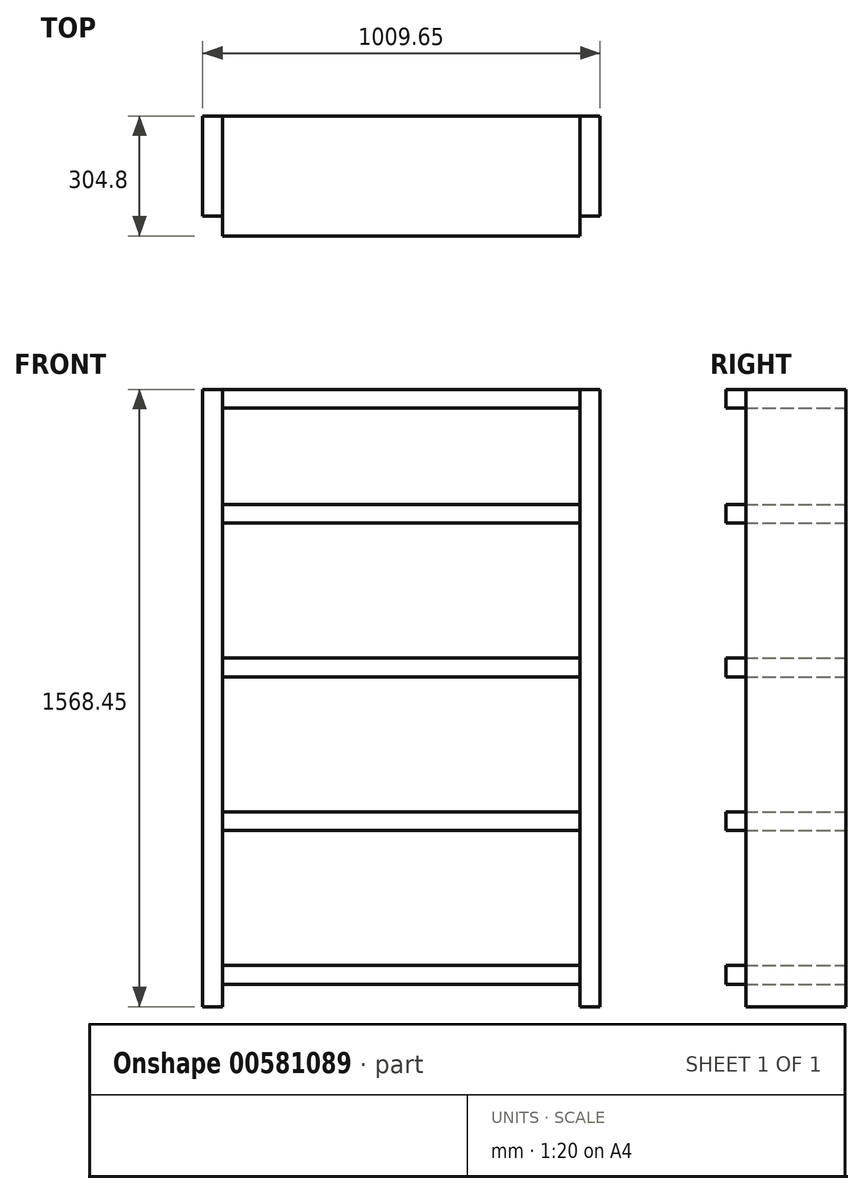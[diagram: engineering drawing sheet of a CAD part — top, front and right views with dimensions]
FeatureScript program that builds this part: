
annotation { "Feature Type Name" : "Feature", "Feature Type Description" : "" }
export const myFeature = defineFeature(function(context is Context, id is Id, definition is map)
    precondition{}
    {
        {
            var Q0;
            Q0=qCreatedBy(makeId("Front.planeOp"),FACE);
            var sketch = newSketch(context, id + "F0", { "sketchPlane" : qUnion([Q0])});
            skLineSegment(sketch, "E0.bottom", {"start": v(-778.9, 353.78) * mm, "end": v(-728.1, 353.78) * mm});
            skLineSegment(sketch, "E0.top", {"start": v(-778.9, -1214.67) * mm, "end": v(-728.1, -1214.67) * mm});
            skLineSegment(sketch, "E0.left", {"start": v(-778.9, 353.78) * mm, "end": v(-778.9, -1214.67) * mm});
            skLineSegment(sketch, "E0.right", {"start": v(-728.1, 353.78) * mm, "end": v(-728.1, -1214.67) * mm});
            skLineSegment(sketch, "E1.bottom", {"start": v(179.95, 353.78) * mm, "end": v(230.75, 353.78) * mm});
            skLineSegment(sketch, "E1.top", {"start": v(179.95, -1214.67) * mm, "end": v(230.75, -1214.67) * mm});
            skLineSegment(sketch, "E1.left", {"start": v(179.95, 353.78) * mm, "end": v(179.95, -1214.67) * mm});
            skLineSegment(sketch, "E1.right", {"start": v(230.75, 353.78) * mm, "end": v(230.75, -1214.67) * mm});
            skLineSegment(sketch, "E2.bottom", {"start": v(-728.1, 353.78) * mm, "end": v(179.95, 353.78) * mm});
            skLineSegment(sketch, "E2.top", {"start": v(-728.1, 306.16) * mm, "end": v(179.95, 306.16) * mm});
            skLineSegment(sketch, "E2.left", {"start": v(-728.1, 353.78) * mm, "end": v(-728.1, 306.16) * mm});
            skLineSegment(sketch, "E2.right", {"start": v(179.95, 353.78) * mm, "end": v(179.95, 306.16) * mm});
            skLineSegment(sketch, "E3.bottom", {"start": v(-728.1, -1109.9) * mm, "end": v(179.95, -1109.9) * mm});
            skLineSegment(sketch, "E3.top", {"start": v(-728.1, -1157.52) * mm, "end": v(179.95, -1157.52) * mm});
            skLineSegment(sketch, "E3.left", {"start": v(-728.1, -1109.9) * mm, "end": v(-728.1, -1157.52) * mm});
            skLineSegment(sketch, "E3.right", {"start": v(179.95, -1109.9) * mm, "end": v(179.95, -1157.52) * mm});
            skLineSegment(sketch, "E4.bottom", {"start": v(-728.1, -719.37) * mm, "end": v(179.95, -719.37) * mm});
            skLineSegment(sketch, "E4.top", {"start": v(-728.1, -767) * mm, "end": v(179.95, -767) * mm});
            skLineSegment(sketch, "E4.left", {"start": v(-728.1, -719.37) * mm, "end": v(-728.1, -767) * mm});
            skLineSegment(sketch, "E4.right", {"start": v(179.95, -719.37) * mm, "end": v(179.95, -767) * mm});
            skLineSegment(sketch, "E5.bottom", {"start": v(-728.1, -328.84) * mm, "end": v(179.95, -328.84) * mm});
            skLineSegment(sketch, "E5.top", {"start": v(-728.1, -376.47) * mm, "end": v(179.95, -376.47) * mm});
            skLineSegment(sketch, "E5.left", {"start": v(-728.1, -328.84) * mm, "end": v(-728.1, -376.47) * mm});
            skLineSegment(sketch, "E5.right", {"start": v(179.95, -328.84) * mm, "end": v(179.95, -376.47) * mm});
            skLineSegment(sketch, "E6.bottom", {"start": v(-728.1, 61.68) * mm, "end": v(179.95, 61.68) * mm});
            skLineSegment(sketch, "E6.top", {"start": v(-728.1, 14.06) * mm, "end": v(179.95, 14.06) * mm});
            skLineSegment(sketch, "E6.left", {"start": v(-728.1, 61.68) * mm, "end": v(-728.1, 14.06) * mm});
            skLineSegment(sketch, "E6.right", {"start": v(179.95, 61.68) * mm, "end": v(179.95, 14.06) * mm});
            skSolve(sketch);
        }
        {
            var Q0;
            Q0=makeQuery(id+"F0.imprint","IMPRINT",FACE,{"disambiguationData":[TD([[makeQuery(id+"F0.imprint","IMPRINT",EDGE,{"derivedFrom":sQuery(id+"F0.wireOp",EDGE,"E0.bottom")}),-1.0]])]});
            var Q1;
            Q1=makeQuery(id+"F0.imprint","IMPRINT",FACE,{"disambiguationData":[TD([[makeQuery(id+"F0.imprint","IMPRINT",EDGE,{"derivedFrom":sQuery(id+"F0.wireOp",EDGE,"E1.bottom")}),-1.0]])]});
            extrude(context, id + "F1", {"entities" : qUnion([Q0, Q1]), "depth" : 254 * mm, "offsetDistance" : 25.4 * mm});
        }
        {
            var Q0;
            Q0=makeQuery(id+"F0.imprint","IMPRINT",FACE,{"disambiguationData":[TD([[makeQuery(id+"F0.imprint","IMPRINT",EDGE,{"derivedFrom":sQuery(id+"F0.wireOp",EDGE,"E2.bottom")}),-1.0]])]});
            var Q1;
            Q1=makeQuery(id+"F0.imprint","IMPRINT",FACE,{"disambiguationData":[TD([[makeQuery(id+"F0.imprint","IMPRINT",EDGE,{"derivedFrom":sQuery(id+"F0.wireOp",EDGE,"E6.bottom")}),-1.0]])]});
            var Q2;
            Q2=makeQuery(id+"F0.imprint","IMPRINT",FACE,{"disambiguationData":[TD([[makeQuery(id+"F0.imprint","IMPRINT",EDGE,{"derivedFrom":sQuery(id+"F0.wireOp",EDGE,"E5.bottom")}),-1.0]])]});
            var Q3;
            Q3=makeQuery(id+"F0.imprint","IMPRINT",FACE,{"disambiguationData":[TD([[makeQuery(id+"F0.imprint","IMPRINT",EDGE,{"derivedFrom":sQuery(id+"F0.wireOp",EDGE,"E4.bottom")}),-1.0]])]});
            var Q4;
            Q4=makeQuery(id+"F0.imprint","IMPRINT",FACE,{"disambiguationData":[TD([[makeQuery(id+"F0.imprint","IMPRINT",EDGE,{"derivedFrom":sQuery(id+"F0.wireOp",EDGE,"E3.bottom")}),-1.0]])]});
            extrude(context, id + "F2", {"entities" : qUnion([Q0, Q1, Q2, Q3, Q4]), "depth" : 304.8 * mm, "offsetDistance" : 25.4 * mm});
        }
    });
